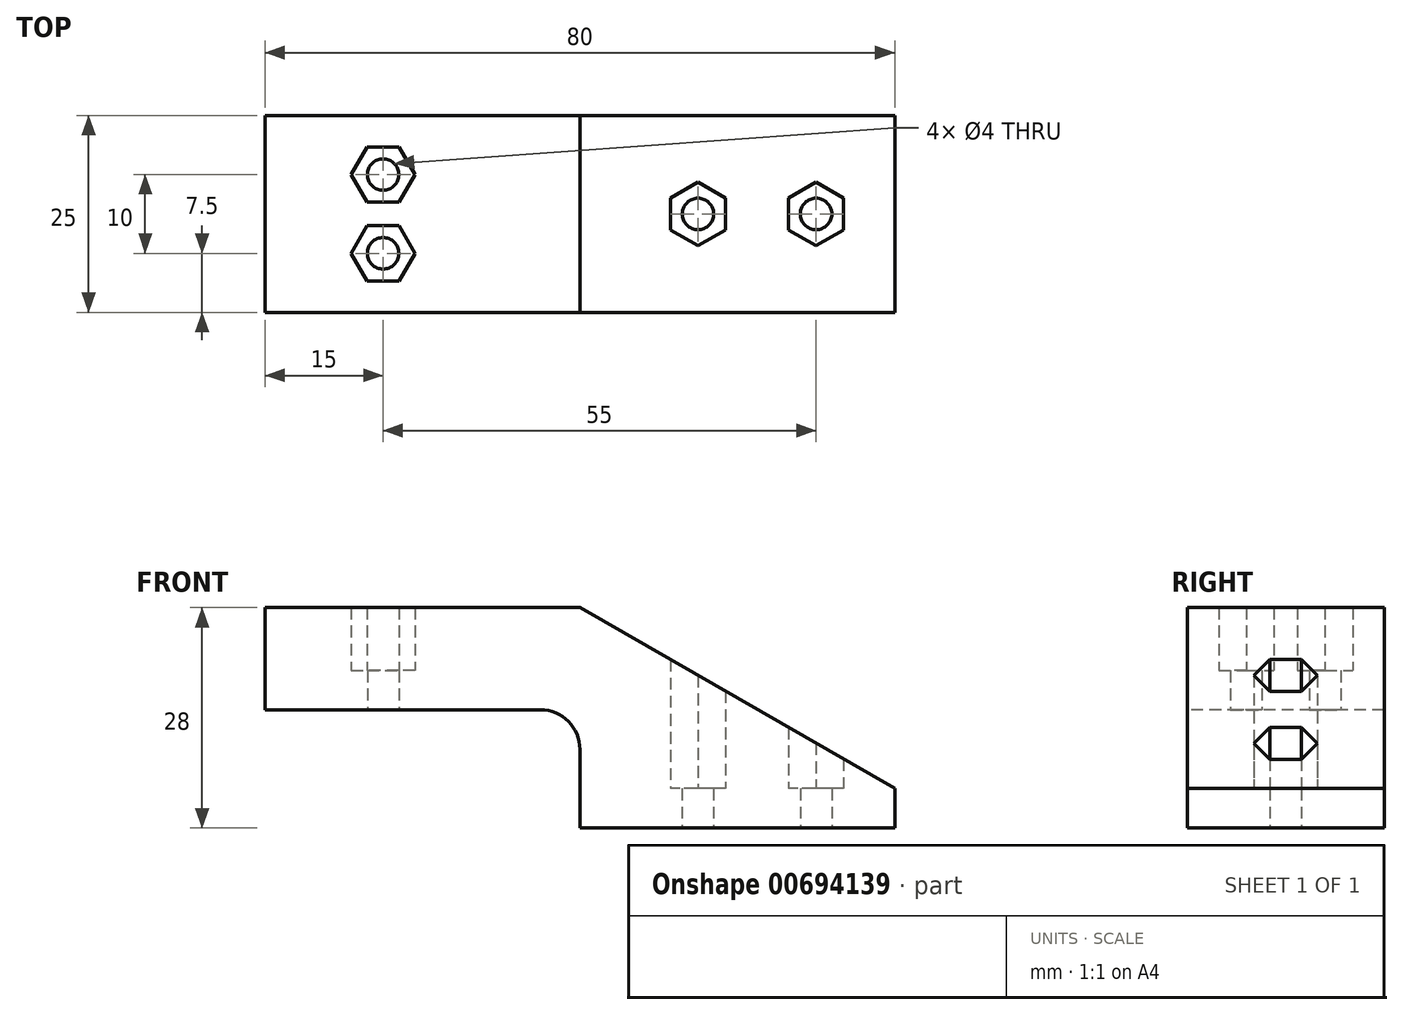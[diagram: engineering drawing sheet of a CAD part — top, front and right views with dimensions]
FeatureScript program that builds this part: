
annotation { "Feature Type Name" : "Feature", "Feature Type Description" : "" }
export const myFeature = defineFeature(function(context is Context, id is Id, definition is map)
    precondition{}
    {
        {
            var Q0;
            Q0=qCreatedBy(makeId("Front.planeOp"),FACE);
            var sketch = newSketch(context, id + "F0", { "sketchPlane" : qUnion([Q0])});
            skLineSegment(sketch, "E0", {"start": v(0, 0) * mm, "end": v(40, 0) * mm});
            skLineSegment(sketch, "E1", {"start": v(40, 0) * mm, "end": v(40, 5) * mm});
            skLineSegment(sketch, "E2", {"start": v(40, 5) * mm, "end": v(0, 28) * mm});
            skLineSegment(sketch, "E3", {"start": v(0, 28) * mm, "end": v(-40, 28) * mm});
            skLineSegment(sketch, "E4", {"start": v(-40, 28) * mm, "end": v(-40, 15) * mm});
            skLineSegment(sketch, "E5", {"start": v(-40, 15) * mm, "end": v(0, 15) * mm});
            skLineSegment(sketch, "E6", {"start": v(0, 15) * mm, "end": v(0, 0) * mm});
            skSolve(sketch);
        }
        {
            var Q0;
            Q0=makeQuery(id+"F0.imprint","IMPRINT",FACE,{"disambiguationData":[TD([[makeQuery(id+"F0.imprint","IMPRINT",EDGE,{"derivedFrom":sQuery(id+"F0.wireOp",EDGE,"E0")}),1.0]])]});
            extrude(context, id + "F1", {"entities" : qUnion([Q0]), "oppositeDirection" : true, "depth" : 25 * mm, "offsetDistance" : 25 * mm});
        }
        {
            var Q0;
            Q0=qCreatedBy(makeId("Top.planeOp"),FACE);
            var sketch = newSketch(context, id + "F2", { "sketchPlane" : qUnion([Q0])});
            skLineSegment(sketch, "E7", {"start": v(0, 0) * mm, "end": v(0, 12.5) * mm, "construction": true});
            skLineSegment(sketch, "E8", {"start": v(0, 12.5) * mm, "end": v(15, 12.5) * mm, "construction": true});
            skLineSegment(sketch, "E9", {"start": v(15, 12.5) * mm, "end": v(30, 12.5) * mm, "construction": true});
            skCircle(sketch, "E10.cCircle", {"center": v(15, 12.5) * mm, "radius": 3.5 * mm, "construction": true});
            skLineSegment(sketch, "E10.0", {"start": v(11.5, 10.48) * mm, "end": v(11.5, 14.52) * mm});
            skLineSegment(sketch, "E10.1", {"start": v(11.5, 14.52) * mm, "end": v(15, 16.54) * mm});
            skLineSegment(sketch, "E10.2", {"start": v(15, 16.54) * mm, "end": v(18.5, 14.52) * mm});
            skLineSegment(sketch, "E10.3", {"start": v(18.5, 14.52) * mm, "end": v(18.5, 10.48) * mm});
            skLineSegment(sketch, "E10.4", {"start": v(18.5, 10.48) * mm, "end": v(15, 8.46) * mm});
            skLineSegment(sketch, "E10.5", {"start": v(15, 8.46) * mm, "end": v(11.5, 10.48) * mm});
            skPoint(sketch, "E10.0.midPoint", {"position": v(11.5, 12.5) * mm});
            skCircle(sketch, "E11.cCircle", {"center": v(30, 12.5) * mm, "radius": 3.5 * mm, "construction": true});
            skLineSegment(sketch, "E11.0", {"start": v(26.5, 10.48) * mm, "end": v(26.5, 14.52) * mm});
            skLineSegment(sketch, "E11.1", {"start": v(26.5, 14.52) * mm, "end": v(30, 16.54) * mm});
            skLineSegment(sketch, "E11.2", {"start": v(30, 16.54) * mm, "end": v(33.5, 14.52) * mm});
            skLineSegment(sketch, "E11.3", {"start": v(33.5, 14.52) * mm, "end": v(33.5, 10.48) * mm});
            skLineSegment(sketch, "E11.4", {"start": v(33.5, 10.48) * mm, "end": v(30, 8.46) * mm});
            skLineSegment(sketch, "E11.5", {"start": v(30, 8.46) * mm, "end": v(26.5, 10.48) * mm});
            skPoint(sketch, "E11.0.midPoint", {"position": v(26.5, 12.5) * mm});
            skCircle(sketch, "E12", {"center": v(15, 12.5) * mm, "radius": 2 * mm});
            skCircle(sketch, "E13", {"center": v(30, 12.5) * mm, "radius": 2 * mm});
            skSolve(sketch);
        }
        {
            var Q0;
            Q0=makeQuery(id+"F2.imprint","IMPRINT",FACE,{"disambiguationData":[TD([[makeQuery(id+"F2.imprint","IMPRINT",EDGE,{"derivedFrom":sQuery(id+"F2.wireOp",EDGE,"E13")}),1.0]])]});
            var Q1;
            Q1=makeQuery(id+"F2.imprint","IMPRINT",FACE,{"disambiguationData":[TD([[makeQuery(id+"F2.imprint","IMPRINT",EDGE,{"derivedFrom":sQuery(id+"F2.wireOp",EDGE,"E12")}),1.0]])]});
            extrude(context, id + "F3", {"entities" : qUnion([Q0, Q1]), "operationType" : NewBodyOperationType.REMOVE, "depth" : 25 * mm, "offsetDistance" : 25 * mm, "hasSecondDirection" : true, "secondDirectionOppositeDirection" : true, "secondDirectionDepth" : 25 * mm});
        }
        {
            var Q0;
            Q0=makeQuery(id+"F2.imprint","IMPRINT",FACE,{"disambiguationData":[TD([[makeQuery(id+"F2.imprint","IMPRINT",EDGE,{"derivedFrom":sQuery(id+"F2.wireOp",EDGE,"E10.0")}),-1.0]])]});
            var Q1;
            Q1=makeQuery(id+"F2.imprint","IMPRINT",FACE,{"disambiguationData":[TD([[makeQuery(id+"F2.imprint","IMPRINT",EDGE,{"derivedFrom":sQuery(id+"F2.wireOp",EDGE,"E11.0")}),-1.0]])]});
            extrude(context, id + "F4", {"entities" : qUnion([Q0, Q1]), "operationType" : NewBodyOperationType.REMOVE, "depth" : 25 * mm, "offsetDistance" : 25 * mm, "hasSecondDirection" : true, "secondDirectionOppositeDirection" : false, "secondDirectionDepth" : 5 * mm});
        }
        {
            var Q0;
            Q0=qCreatedBy(makeId("Top.planeOp"),FACE);
            var sketch = newSketch(context, id + "F5", { "sketchPlane" : qUnion([Q0])});
            skLineSegment(sketch, "E14", {"start": v(0, 0) * mm, "end": v(0, 12.5) * mm, "construction": true});
            skLineSegment(sketch, "E15", {"start": v(0, 12.5) * mm, "end": v(-25, 12.5) * mm, "construction": true});
            skLineSegment(sketch, "E16", {"start": v(-25, 12.5) * mm, "end": v(-25, 7.5) * mm, "construction": true});
            skLineSegment(sketch, "E17", {"start": v(-25, 7.5) * mm, "end": v(-25, 17.5) * mm, "construction": true});
            skCircle(sketch, "E18.cCircle", {"center": v(-25, 17.5) * mm, "radius": 3.5 * mm, "construction": true});
            skLineSegment(sketch, "E18.0", {"start": v(-27.02, 21) * mm, "end": v(-22.98, 21) * mm});
            skLineSegment(sketch, "E18.1", {"start": v(-22.98, 21) * mm, "end": v(-20.96, 17.5) * mm});
            skLineSegment(sketch, "E18.2", {"start": v(-20.96, 17.5) * mm, "end": v(-22.98, 14) * mm});
            skLineSegment(sketch, "E18.3", {"start": v(-22.98, 14) * mm, "end": v(-27.02, 14) * mm});
            skLineSegment(sketch, "E18.4", {"start": v(-27.02, 14) * mm, "end": v(-29.04, 17.5) * mm});
            skLineSegment(sketch, "E18.5", {"start": v(-29.04, 17.5) * mm, "end": v(-27.02, 21) * mm});
            skPoint(sketch, "E18.0.midPoint", {"position": v(-25, 21) * mm});
            skCircle(sketch, "E19.cCircle", {"center": v(-25, 7.5) * mm, "radius": 3.5 * mm, "construction": true});
            skLineSegment(sketch, "E19.0", {"start": v(-27.02, 11) * mm, "end": v(-22.98, 11) * mm});
            skLineSegment(sketch, "E19.1", {"start": v(-22.98, 11) * mm, "end": v(-20.96, 7.5) * mm});
            skLineSegment(sketch, "E19.2", {"start": v(-20.96, 7.5) * mm, "end": v(-22.98, 4) * mm});
            skLineSegment(sketch, "E19.3", {"start": v(-22.98, 4) * mm, "end": v(-27.02, 4) * mm});
            skLineSegment(sketch, "E19.4", {"start": v(-27.02, 4) * mm, "end": v(-29.04, 7.5) * mm});
            skLineSegment(sketch, "E19.5", {"start": v(-29.04, 7.5) * mm, "end": v(-27.02, 11) * mm});
            skPoint(sketch, "E19.0.midPoint", {"position": v(-25, 11) * mm});
            skCircle(sketch, "E20", {"center": v(-25, 17.5) * mm, "radius": 2 * mm});
            skCircle(sketch, "E21", {"center": v(-25, 7.5) * mm, "radius": 2 * mm});
            skSolve(sketch);
        }
        {
            var Q0;
            Q0 = qSketchRegion(id + "F5", true);
            extrude(context, id + "F6", {"entities" : qUnion([Q0]), "operationType" : NewBodyOperationType.REMOVE, "depth" : 40 * mm, "offsetDistance" : 25 * mm, "hasSecondDirection" : true, "secondDirectionOppositeDirection" : false, "secondDirectionDepth" : 20 * mm});
        }
        {
            var Q0;
            Q0=makeQuery(id+"F5.imprint","IMPRINT",FACE,{"disambiguationData":[TD([[makeQuery(id+"F5.imprint","IMPRINT",EDGE,{"derivedFrom":sQuery(id+"F5.wireOp",EDGE,"E21")}),1.0]])]});
            var Q1;
            Q1=makeQuery(id+"F5.imprint","IMPRINT",FACE,{"disambiguationData":[TD([[makeQuery(id+"F5.imprint","IMPRINT",EDGE,{"derivedFrom":sQuery(id+"F5.wireOp",EDGE,"E20")}),1.0]])]});
            extrude(context, id + "F7", {"entities" : qUnion([Q0, Q1]), "operationType" : NewBodyOperationType.REMOVE, "depth" : 40 * mm, "offsetDistance" : 25 * mm});
        }
        {
            var Q0;
            Q0=makeQuery(id+"F1.opExtrude","SWEPT_EDGE",EDGE,{"disambiguationData":[OSD([sQuery(id+"F0.wireOp",EDGE,"E5"),sQuery(id+"F0.wireOp",EDGE,"E6")])]});
            fillet(context, id + "F8", {"entities" : qUnion([Q0]), "radius" : 5 * mm, "tangentPropagation" : true, "allowEdgeOverflow" : false});
        }
    });
